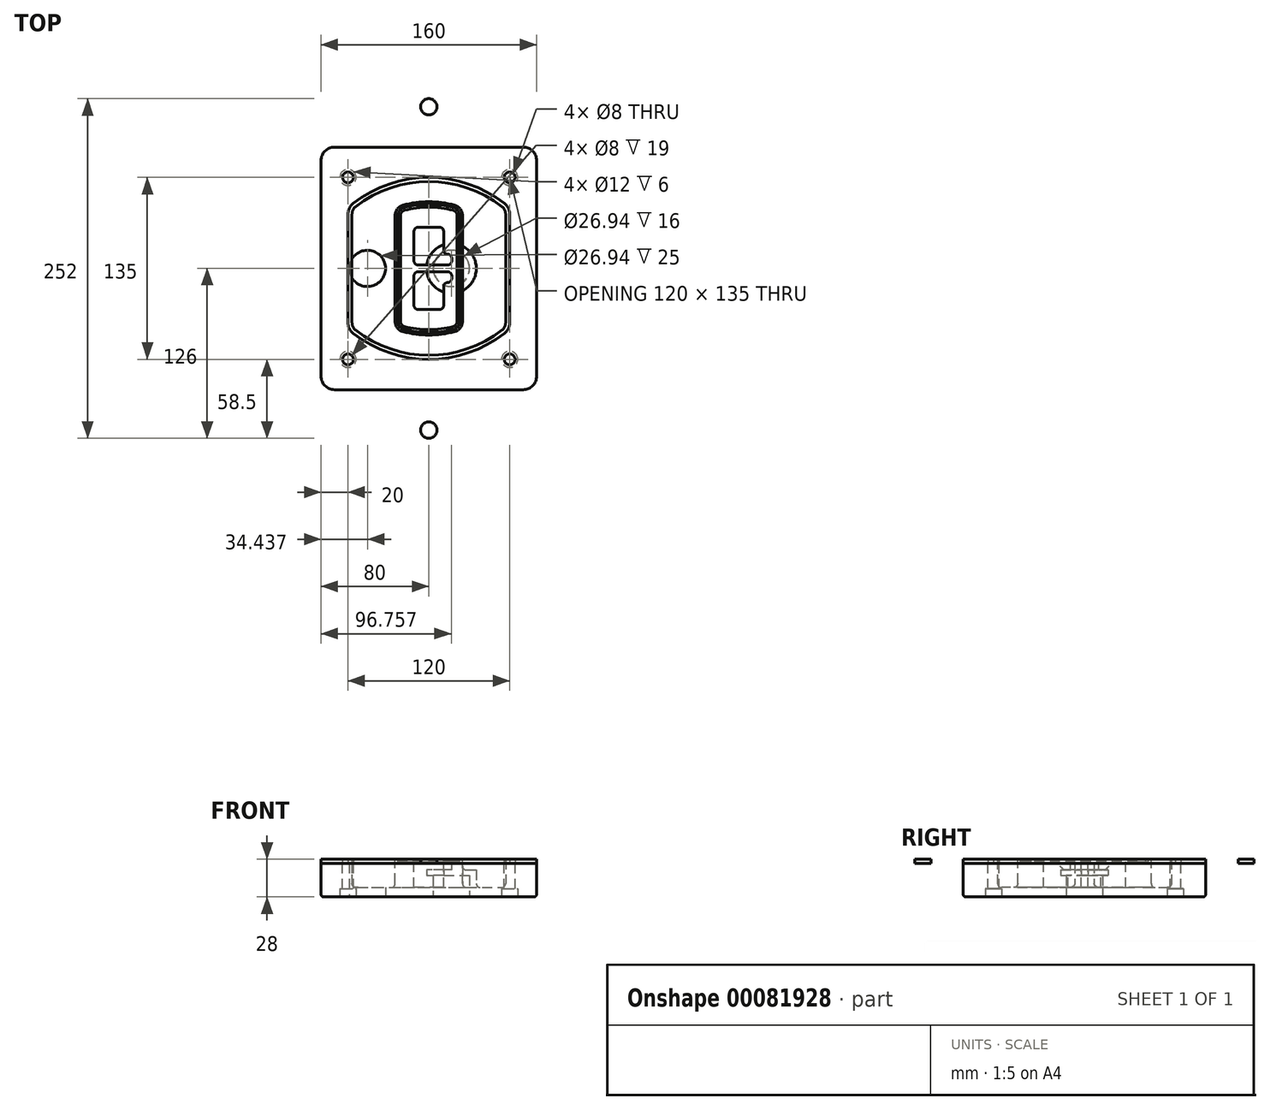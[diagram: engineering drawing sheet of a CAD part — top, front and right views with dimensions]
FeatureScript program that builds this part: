
annotation { "Feature Type Name" : "Feature", "Feature Type Description" : "" }
export const myFeature = defineFeature(function(context is Context, id is Id, definition is map)
    precondition{}
    {
        {
            var Q0;
            Q0=qCreatedBy(makeId("Top.planeOp"),FACE);
            var sketch = newSketch(context, id + "F0", { "sketchPlane" : qUnion([Q0])});
            skPoint(sketch, "E0.rect.middle", {"position": v(0, 0) * mm});
            skLineSegment(sketch, "E1.bottom", {"start": v(-70, -90) * mm, "end": v(70, -90) * mm});
            skLineSegment(sketch, "E1.top", {"start": v(-70, 90) * mm, "end": v(70, 90) * mm});
            skLineSegment(sketch, "E1.left", {"start": v(-80, -80) * mm, "end": v(-80, 80) * mm});
            skLineSegment(sketch, "E1.right", {"start": v(80, -80) * mm, "end": v(80, 80) * mm});
            skLineSegment(sketch, "E2", {"start": v(-80, 90) * mm, "end": v(80, -90) * mm, "construction": true});
            skLineSegment(sketch, "E3", {"start": v(80, 90) * mm, "end": v(-80, -90) * mm, "construction": true});
            skCircle(sketch, "E4", {"center": v(-60, 67.5) * mm, "radius": 4 * mm});
            skCircle(sketch, "E5", {"center": v(60, 67.5) * mm, "radius": 4 * mm});
            skCircle(sketch, "E6", {"center": v(60, -67.5) * mm, "radius": 4 * mm});
            skCircle(sketch, "E7", {"center": v(-60, -67.5) * mm, "radius": 4 * mm});
            skLineSegment(sketch, "E8", {"start": v(-60, 67.5) * mm, "end": v(60, 67.5) * mm, "construction": true});
            skLineSegment(sketch, "E9", {"start": v(60, 67.5) * mm, "end": v(60, -67.5) * mm, "construction": true});
            skLineSegment(sketch, "E10", {"start": v(60, -67.5) * mm, "end": v(-60, -67.5) * mm, "construction": true});
            skLineSegment(sketch, "E11", {"start": v(-60, -67.5) * mm, "end": v(-60, 67.5) * mm, "construction": true});
            skLineSegment(sketch, "E12", {"start": v(-60, 40.3) * mm, "end": v(-60, -40.3) * mm});
            skLineSegment(sketch, "E13", {"start": v(60, 40.3) * mm, "end": v(60, -40.3) * mm});
            skArc(sketch, "E14", {"start": v(56.15, 48.18) * mm, "mid": v(0, 67.5) * mm, "end": v(-56.15, 48.18) * mm});
            skArc(sketch, "E15", {"start": v(-56.15, -48.18) * mm, "mid": v(0, -67.5) * mm, "end": v(56.15, -48.18) * mm});
            skLineSegment(sketch, "E16", {"start": v(-60, 0) * mm, "end": v(60, 0) * mm, "construction": true});
            skPoint(sketch, "E17.visualSharp", {"position": v(-60, -45) * mm});
            skArc(sketch, "E17.filletArc", {"start": v(-60, -40.3) * mm, "mid": v(-58.99, -44.68) * mm, "end": v(-56.15, -48.18) * mm});
            skPoint(sketch, "E18.visualSharp", {"position": v(-60, 45) * mm});
            skArc(sketch, "E18.filletArc", {"start": v(-56.15, 48.18) * mm, "mid": v(-58.99, 44.68) * mm, "end": v(-60, 40.3) * mm});
            skPoint(sketch, "E19.visualSharp", {"position": v(60, 45) * mm});
            skArc(sketch, "E19.filletArc", {"start": v(60, 40.3) * mm, "mid": v(58.99, 44.68) * mm, "end": v(56.15, 48.18) * mm});
            skPoint(sketch, "E20.visualSharp", {"position": v(60, -45) * mm});
            skArc(sketch, "E20.filletArc", {"start": v(56.15, -48.18) * mm, "mid": v(58.99, -44.68) * mm, "end": v(60, -40.3) * mm});
            skPoint(sketch, "E21.visualSharp", {"position": v(-80, 90) * mm});
            skArc(sketch, "E21.filletArc", {"start": v(-70, 90) * mm, "mid": v(-77.07, 87.07) * mm, "end": v(-80, 80) * mm});
            skPoint(sketch, "E22.visualSharp", {"position": v(80, 90) * mm});
            skArc(sketch, "E22.filletArc", {"start": v(80, 80) * mm, "mid": v(77.07, 87.07) * mm, "end": v(70, 90) * mm});
            skPoint(sketch, "E23.visualSharp", {"position": v(80, -90) * mm});
            skArc(sketch, "E23.filletArc", {"start": v(70, -90) * mm, "mid": v(77.07, -87.07) * mm, "end": v(80, -80) * mm});
            skPoint(sketch, "E24.visualSharp", {"position": v(-80, -90) * mm});
            skArc(sketch, "E24.filletArc", {"start": v(-80, -80) * mm, "mid": v(-77.07, -87.07) * mm, "end": v(-70, -90) * mm});
            skArc(sketch, "E25.0", {"start": v(57, 40.3) * mm, "mid": v(56.3, 43.36) * mm, "end": v(54.3, 45.81) * mm});
            skLineSegment(sketch, "E25.1", {"start": v(57, 40.3) * mm, "end": v(57, -40.3) * mm});
            skArc(sketch, "E25.2", {"start": v(54.3, -45.81) * mm, "mid": v(56.3, -43.36) * mm, "end": v(57, -40.3) * mm});
            skArc(sketch, "E25.3", {"start": v(-54.3, -45.81) * mm, "mid": v(0, -64.5) * mm, "end": v(54.3, -45.81) * mm});
            skArc(sketch, "E25.4", {"start": v(-57, -40.3) * mm, "mid": v(-56.3, -43.36) * mm, "end": v(-54.3, -45.81) * mm});
            skArc(sketch, "E25.5", {"start": v(54.3, 45.81) * mm, "mid": v(0, 64.5) * mm, "end": v(-54.3, 45.81) * mm});
            skLineSegment(sketch, "E25.6", {"start": v(-57, 40.3) * mm, "end": v(-57, -40.3) * mm});
            skArc(sketch, "E25.7", {"start": v(-54.3, 45.81) * mm, "mid": v(-56.3, 43.36) * mm, "end": v(-57, 40.3) * mm});
            skArc(sketch, "E26.0", {"start": v(-58.62, 51.33) * mm, "mid": v(-62.58, 46.43) * mm, "end": v(-64, 40.3) * mm});
            skArc(sketch, "E26.1", {"start": v(58.62, 51.33) * mm, "mid": v(0, 71.5) * mm, "end": v(-58.62, 51.33) * mm});
            skArc(sketch, "E26.2", {"start": v(64, 40.3) * mm, "mid": v(62.58, 46.43) * mm, "end": v(58.62, 51.33) * mm});
            skLineSegment(sketch, "E26.3", {"start": v(64, 40.3) * mm, "end": v(64, -40.3) * mm});
            skArc(sketch, "E26.4", {"start": v(58.62, -51.33) * mm, "mid": v(62.58, -46.43) * mm, "end": v(64, -40.3) * mm});
            skLineSegment(sketch, "E26.5", {"start": v(-64, 40.3) * mm, "end": v(-64, -40.3) * mm});
            skArc(sketch, "E26.6", {"start": v(-58.62, -51.33) * mm, "mid": v(0, -71.5) * mm, "end": v(58.62, -51.33) * mm});
            skArc(sketch, "E26.7", {"start": v(-64, -40.3) * mm, "mid": v(-62.58, -46.43) * mm, "end": v(-58.62, -51.33) * mm});
            skSolve(sketch);
        }
        {
            var Q0;
            Q0=makeQuery(id+"F0.imprint","IMPRINT",FACE,{"disambiguationData":[TD([[makeQuery(id+"F0.imprint","IMPRINT",EDGE,{"derivedFrom":sQuery(id+"F0.wireOp",EDGE,"E1.bottom")}),1.0]])]});
            var Q1;
            Q1=makeQuery(id+"F0.imprint","IMPRINT",FACE,{"disambiguationData":[TD([[makeQuery(id+"F0.imprint","IMPRINT",EDGE,{"derivedFrom":sQuery(id+"F0.wireOp",EDGE,"E12")}),1.0]])]});
            var Q2;
            Q2=makeQuery(id+"F0.imprint","IMPRINT",FACE,{"disambiguationData":[TD([[makeQuery(id+"F0.imprint","IMPRINT",EDGE,{"derivedFrom":sQuery(id+"F0.wireOp",EDGE,"E25.0")}),1.0]])]});
            var Q3;
            Q3=makeQuery(id+"F0.imprint","IMPRINT",FACE,{"disambiguationData":[TD([[makeQuery(id+"F0.imprint","IMPRINT",EDGE,{"derivedFrom":sQuery(id+"F0.wireOp",EDGE,"E12")}),-1.0]])]});
            extrude(context, id + "F1", {"entities" : qUnion([Q0, Q1, Q2, Q3]), "oppositeDirection" : true, "depth" : 25 * mm});
        }
        {
            var Q0;
            Q0=makeQuery(id+"F0.imprint","IMPRINT",FACE,{"disambiguationData":[TD([[makeQuery(id+"F0.imprint","IMPRINT",EDGE,{"derivedFrom":sQuery(id+"F0.wireOp",EDGE,"E12")}),1.0]])]});
            extrude(context, id + "F2", {"entities" : qUnion([Q0]), "operationType" : NewBodyOperationType.ADD, "depth" : 3 * mm});
        }
        {
            var Q0;
            Q0=makeQuery(id+"F0.imprint","IMPRINT",FACE,{"disambiguationData":[TD([[makeQuery(id+"F0.imprint","IMPRINT",EDGE,{"derivedFrom":sQuery(id+"F0.wireOp",EDGE,"E25.0")}),1.0]])]});
            extrude(context, id + "F3", {"entities" : qUnion([Q0]), "operationType" : NewBodyOperationType.REMOVE, "oppositeDirection" : true, "depth" : 18 * mm});
        }
        {
            var Q0;
            Q0=makeQuery(id+"F2.opExtrude","CAP_FACE",FACE,{"disambiguationData":[OSD([sQuery(id+"F0.wireOp",EDGE,"E12"),sQuery(id+"F0.wireOp",EDGE,"E13"),sQuery(id+"F0.wireOp",EDGE,"E14"),sQuery(id+"F0.wireOp",EDGE,"E15"),sQuery(id+"F0.wireOp",EDGE,"E17.filletArc"),sQuery(id+"F0.wireOp",EDGE,"E18.filletArc"),sQuery(id+"F0.wireOp",EDGE,"E19.filletArc"),sQuery(id+"F0.wireOp",EDGE,"E20.filletArc"),sQuery(id+"F0.wireOp",EDGE,"E25.0"),sQuery(id+"F0.wireOp",EDGE,"E25.1"),sQuery(id+"F0.wireOp",EDGE,"E25.2"),sQuery(id+"F0.wireOp",EDGE,"E25.3"),sQuery(id+"F0.wireOp",EDGE,"E25.4"),sQuery(id+"F0.wireOp",EDGE,"E25.5"),sQuery(id+"F0.wireOp",EDGE,"E25.6"),sQuery(id+"F0.wireOp",EDGE,"E25.7")])],"isStart":false});
            var sketch = newSketch(context, id + "F4", { "sketchPlane" : qUnion([Q0])});
            skArc(sketch, "E27.0", {"start": v(-19.08, -46.97) * mm, "mid": v(0, -49.5) * mm, "end": v(19.08, -46.97) * mm});
            skArc(sketch, "E28.0", {"start": v(19.08, 46.97) * mm, "mid": v(0, 49.5) * mm, "end": v(-19.08, 46.97) * mm});
            skLineSegment(sketch, "E29", {"start": v(-25, 39.25) * mm, "end": v(-25, -39.25) * mm});
            skLineSegment(sketch, "E30", {"start": v(25, 39.25) * mm, "end": v(25, -39.25) * mm});
            skLineSegment(sketch, "E31", {"start": v(-25, 45.1) * mm, "end": v(25, 45.1) * mm, "construction": true});
            skLineSegment(sketch, "E32", {"start": v(-25, -45.1) * mm, "end": v(25, -45.1) * mm, "construction": true});
            skPoint(sketch, "E33.visualSharp", {"position": v(-25, 45.1) * mm});
            skArc(sketch, "E33.filletArc", {"start": v(-19.08, 46.97) * mm, "mid": v(-23.35, 44.11) * mm, "end": v(-25, 39.25) * mm});
            skPoint(sketch, "E34.visualSharp", {"position": v(25, 45.1) * mm});
            skArc(sketch, "E34.filletArc", {"start": v(25, 39.25) * mm, "mid": v(23.35, 44.11) * mm, "end": v(19.08, 46.97) * mm});
            skPoint(sketch, "E35.visualSharp", {"position": v(25, -45.1) * mm});
            skArc(sketch, "E35.filletArc", {"start": v(19.08, -46.97) * mm, "mid": v(23.35, -44.11) * mm, "end": v(25, -39.25) * mm});
            skPoint(sketch, "E36.visualSharp", {"position": v(-25, -45.1) * mm});
            skArc(sketch, "E36.filletArc", {"start": v(-25, -39.25) * mm, "mid": v(-23.35, -44.11) * mm, "end": v(-19.08, -46.97) * mm});
            skArc(sketch, "E37.0", {"start": v(54.3, 45.81) * mm, "mid": v(0, 64.5) * mm, "end": v(-54.3, 45.81) * mm});
            skArc(sketch, "E37.1", {"start": v(-54.3, 45.81) * mm, "mid": v(-56.3, 43.36) * mm, "end": v(-57, 40.3) * mm});
            skLineSegment(sketch, "E37.2", {"start": v(-57, 40.3) * mm, "end": v(-57, -40.3) * mm});
            skArc(sketch, "E37.3", {"start": v(-57, -40.3) * mm, "mid": v(-56.3, -43.36) * mm, "end": v(-54.3, -45.81) * mm});
            skArc(sketch, "E37.4", {"start": v(-54.3, -45.81) * mm, "mid": v(0, -64.5) * mm, "end": v(54.3, -45.81) * mm});
            skArc(sketch, "E37.5", {"start": v(54.3, -45.81) * mm, "mid": v(56.3, -43.36) * mm, "end": v(57, -40.3) * mm});
            skLineSegment(sketch, "E37.6", {"start": v(57, 40.3) * mm, "end": v(57, -40.3) * mm});
            skArc(sketch, "E37.7", {"start": v(57, 40.3) * mm, "mid": v(56.3, 43.36) * mm, "end": v(54.3, 45.81) * mm});
            skLineSegment(sketch, "E38.0", {"start": v(23, 39.25) * mm, "end": v(23, -39.25) * mm});
            skArc(sketch, "E38.1", {"start": v(18.56, -45.04) * mm, "mid": v(21.76, -42.9) * mm, "end": v(23, -39.25) * mm});
            skArc(sketch, "E38.2", {"start": v(-18.56, -45.04) * mm, "mid": v(0, -47.5) * mm, "end": v(18.56, -45.04) * mm});
            skArc(sketch, "E38.3", {"start": v(-23, -39.25) * mm, "mid": v(-21.76, -42.9) * mm, "end": v(-18.56, -45.04) * mm});
            skLineSegment(sketch, "E38.4", {"start": v(-23, 39.25) * mm, "end": v(-23, -39.25) * mm});
            skArc(sketch, "E38.5", {"start": v(23, 39.25) * mm, "mid": v(21.76, 42.9) * mm, "end": v(18.56, 45.04) * mm});
            skArc(sketch, "E38.6", {"start": v(-18.56, 45.04) * mm, "mid": v(-21.76, 42.9) * mm, "end": v(-23, 39.25) * mm});
            skArc(sketch, "E38.7", {"start": v(18.56, 45.04) * mm, "mid": v(0, 47.5) * mm, "end": v(-18.56, 45.04) * mm});
            skArc(sketch, "E39.0", {"start": v(21, 39.25) * mm, "mid": v(20.18, 41.68) * mm, "end": v(18.04, 43.1) * mm});
            skLineSegment(sketch, "E39.1", {"start": v(21, 39.25) * mm, "end": v(21, -39.25) * mm});
            skArc(sketch, "E39.2", {"start": v(18.04, -43.1) * mm, "mid": v(20.18, -41.68) * mm, "end": v(21, -39.25) * mm});
            skArc(sketch, "E39.3", {"start": v(-18.04, -43.1) * mm, "mid": v(0, -45.5) * mm, "end": v(18.04, -43.1) * mm});
            skArc(sketch, "E39.4", {"start": v(-21, -39.25) * mm, "mid": v(-20.18, -41.68) * mm, "end": v(-18.04, -43.1) * mm});
            skArc(sketch, "E39.5", {"start": v(18.04, 43.1) * mm, "mid": v(0, 45.5) * mm, "end": v(-18.04, 43.1) * mm});
            skLineSegment(sketch, "E39.6", {"start": v(-21, 39.25) * mm, "end": v(-21, -39.25) * mm});
            skArc(sketch, "E39.7", {"start": v(-18.04, 43.1) * mm, "mid": v(-20.18, 41.68) * mm, "end": v(-21, 39.25) * mm});
            skLineSegment(sketch, "E40", {"start": v(-25, 0) * mm, "end": v(25, 0) * mm, "construction": true});
            skLineSegment(sketch, "E41", {"start": v(-11, 5.5) * mm, "end": v(-11, 27.5) * mm});
            skLineSegment(sketch, "E42", {"start": v(-8, 30.5) * mm, "end": v(8, 30.5) * mm});
            skLineSegment(sketch, "E43", {"start": v(11, 27.5) * mm, "end": v(11, 13.5) * mm});
            skLineSegment(sketch, "E44", {"start": v(14, 10.5) * mm, "end": v(14, 10.5) * mm});
            skLineSegment(sketch, "E45", {"start": v(17, 7.5) * mm, "end": v(17, 5.5) * mm});
            skLineSegment(sketch, "E46", {"start": v(14, 2.5) * mm, "end": v(-8, 2.5) * mm});
            skPoint(sketch, "E47.visualSharp", {"position": v(-11, 30.5) * mm});
            skArc(sketch, "E47.filletArc", {"start": v(-8, 30.5) * mm, "mid": v(-10.12, 29.62) * mm, "end": v(-11, 27.5) * mm});
            skPoint(sketch, "E48.visualSharp", {"position": v(11, 30.5) * mm});
            skArc(sketch, "E48.filletArc", {"start": v(11, 27.5) * mm, "mid": v(10.12, 29.62) * mm, "end": v(8, 30.5) * mm});
            skPoint(sketch, "E49.visualSharp", {"position": v(11, 10.5) * mm});
            skArc(sketch, "E49.filletArc", {"start": v(11, 13.5) * mm, "mid": v(11.88, 11.38) * mm, "end": v(14, 10.5) * mm});
            skPoint(sketch, "E50.visualSharp", {"position": v(17, 10.5) * mm});
            skArc(sketch, "E50.filletArc", {"start": v(17, 7.5) * mm, "mid": v(16.12, 9.62) * mm, "end": v(14, 10.5) * mm});
            skPoint(sketch, "E51.visualSharp", {"position": v(17, 2.5) * mm});
            skArc(sketch, "E51.filletArc", {"start": v(14, 2.5) * mm, "mid": v(16.12, 3.38) * mm, "end": v(17, 5.5) * mm});
            skPoint(sketch, "E52.visualSharp", {"position": v(-11, 2.5) * mm});
            skArc(sketch, "E52.filletArc", {"start": v(-11, 5.5) * mm, "mid": v(-10.12, 3.38) * mm, "end": v(-8, 2.5) * mm});
            skLineSegment(sketch, "E53.0.MirrorCS", {"start": v(14, -2.5) * mm, "end": v(-8, -2.5) * mm});
            skArc(sketch, "E54.0.MirrorCS", {"start": v(-11, -5.5) * mm, "mid": v(-10.12, -3.38) * mm, "end": v(-8, -2.5) * mm});
            skLineSegment(sketch, "E55.0.MirrorCS", {"start": v(-11, -5.5) * mm, "end": v(-11, -27.5) * mm});
            skArc(sketch, "E56.0.MirrorCS", {"start": v(-8, -30.5) * mm, "mid": v(-10.12, -29.62) * mm, "end": v(-11, -27.5) * mm});
            skLineSegment(sketch, "E57.0.MirrorCS", {"start": v(-8, -30.5) * mm, "end": v(8, -30.5) * mm});
            skArc(sketch, "E58.0.MirrorCS", {"start": v(11, -27.5) * mm, "mid": v(10.12, -29.62) * mm, "end": v(8, -30.5) * mm});
            skLineSegment(sketch, "E59.0.MirrorCS", {"start": v(11, -27.5) * mm, "end": v(11, -13.5) * mm});
            skArc(sketch, "E60.0.MirrorCS", {"start": v(11, -13.5) * mm, "mid": v(11.88, -11.38) * mm, "end": v(14, -10.5) * mm});
            skArc(sketch, "E61.0.MirrorCS", {"start": v(17, -7.5) * mm, "mid": v(16.12, -9.62) * mm, "end": v(14, -10.5) * mm});
            skLineSegment(sketch, "E62.0.MirrorCS", {"start": v(17, -7.5) * mm, "end": v(17, -5.5) * mm});
            skArc(sketch, "E63.0.MirrorCS", {"start": v(14, -2.5) * mm, "mid": v(16.12, -3.38) * mm, "end": v(17, -5.5) * mm});
            skSolve(sketch);
        }
        {
            var Q0;
            Q0=makeQuery(id+"F4.imprint","IMPRINT",FACE,{"disambiguationData":[TD([[makeQuery(id+"F4.imprint","IMPRINT",EDGE,{"derivedFrom":sQuery(id+"F4.wireOp",EDGE,"E27.0")}),1.0]])]});
            var Q1;
            Q1=makeQuery(id+"F4.imprint","IMPRINT",FACE,{"disambiguationData":[TD([[makeQuery(id+"F4.imprint","IMPRINT",EDGE,{"derivedFrom":sQuery(id+"F4.wireOp",EDGE,"E38.0")}),-1.0]])]});
            var Q2;
            Q2=makeQuery(id+"F4.imprint","IMPRINT",FACE,{"disambiguationData":[TD([[makeQuery(id+"F4.imprint","IMPRINT",EDGE,{"derivedFrom":sQuery(id+"F4.wireOp",EDGE,"E39.0")}),1.0]])]});
            extrude(context, id + "F5", {"entities" : qUnion([Q0, Q1, Q2]), "operationType" : NewBodyOperationType.ADD, "endBound" : BoundingType.UP_TO_NEXT, "oppositeDirection" : true, "depth" : 25 * mm});
        }
        {
            var Q0;
            Q0=makeQuery(id+"F4.imprint","IMPRINT",FACE,{"disambiguationData":[TD([[makeQuery(id+"F4.imprint","IMPRINT",EDGE,{"derivedFrom":sQuery(id+"F4.wireOp",EDGE,"E38.0")}),-1.0]])]});
            extrude(context, id + "F6", {"entities" : qUnion([Q0]), "operationType" : NewBodyOperationType.REMOVE, "oppositeDirection" : true, "depth" : 2 * mm});
        }
        {
            var Q0;
            Q0=makeQuery(id+"F1.opExtrude","CAP_FACE",FACE,{"disambiguationData":[OSD([sQuery(id+"F0.wireOp",EDGE,"E1.bottom"),sQuery(id+"F0.wireOp",EDGE,"E1.top"),sQuery(id+"F0.wireOp",EDGE,"E1.left"),sQuery(id+"F0.wireOp",EDGE,"E1.right"),sQuery(id+"F0.wireOp",EDGE,"E4"),sQuery(id+"F0.wireOp",EDGE,"E5"),sQuery(id+"F0.wireOp",EDGE,"E6"),sQuery(id+"F0.wireOp",EDGE,"E7"),sQuery(id+"F0.wireOp",EDGE,"E21.filletArc"),sQuery(id+"F0.wireOp",EDGE,"E22.filletArc"),sQuery(id+"F0.wireOp",EDGE,"E23.filletArc"),sQuery(id+"F0.wireOp",EDGE,"E24.filletArc")])],"isStart":false});
            var sketch = newSketch(context, id + "F7", { "sketchPlane" : qUnion([Q0])});
            skCircle(sketch, "E64", {"center": v(16.76, 0) * mm, "radius": 13.47 * mm});
            skCircle(sketch, "E65", {"center": v(-45.56, 0) * mm, "radius": 13.47 * mm});
            skLineSegment(sketch, "E66", {"start": v(80, 0) * mm, "end": v(-80, 0) * mm});
            skCircle(sketch, "E67", {"center": v(16.76, 0) * mm, "radius": 18.47 * mm});
            skCircle(sketch, "E68", {"center": v(60, -67.5) * mm, "radius": 6 * mm});
            skCircle(sketch, "E69", {"center": v(-60, -67.5) * mm, "radius": 6 * mm});
            skCircle(sketch, "E70", {"center": v(-60, 67.5) * mm, "radius": 6 * mm});
            skCircle(sketch, "E71", {"center": v(60, 67.5) * mm, "radius": 6 * mm});
            skSolve(sketch);
        }
        {
            var Q0;
            {var subQ1=sQuery(id+"F7.wireOp",EDGE,"E66");var subQ4=sQuery(id+"F7.wireOp",EDGE,"E64");var subQ6=makeQuery(id+"F7.imprint","INTERSECT",VERTEX,{"disambiguationData":[OD(0.0)],"derivedFrom":[subQ4,subQ1]});Q0=makeQuery(id+"F7.imprint","IMPRINT",FACE,{"disambiguationData":[TD([[makeQuery(id+"F7.imprint","IMPRINT",EDGE,{"disambiguationData":[TD([[subQ6,-1.0]])],"derivedFrom":subQ4}),-1.0]])]});}
            var Q1;
            {var subQ0=sQuery(id+"F7.wireOp",EDGE,"E66");var subQ1=sQuery(id+"F7.wireOp",EDGE,"E64");var subQ3=makeQuery(id+"F7.imprint","INTERSECT",VERTEX,{"disambiguationData":[OD(0.0)],"derivedFrom":[subQ1,subQ0]});Q1=makeQuery(id+"F7.imprint","IMPRINT",FACE,{"disambiguationData":[TD([[makeQuery(id+"F7.imprint","IMPRINT",EDGE,{"disambiguationData":[TD([[subQ3,-1.0]])],"derivedFrom":subQ1}),1.0]])]});}
            var Q2;
            {var subQ0=sQuery(id+"F7.wireOp",EDGE,"E66");var subQ1=sQuery(id+"F7.wireOp",EDGE,"E64");var subQ3=makeQuery(id+"F7.imprint","INTERSECT",VERTEX,{"disambiguationData":[OD(0.0)],"derivedFrom":[subQ1,subQ0]});Q2=makeQuery(id+"F7.imprint","IMPRINT",FACE,{"disambiguationData":[TD([[makeQuery(id+"F7.imprint","IMPRINT",EDGE,{"disambiguationData":[TD([[subQ3,1.0]])],"derivedFrom":subQ1}),1.0]])]});}
            var Q3;
            {var subQ1=sQuery(id+"F7.wireOp",EDGE,"E66");var subQ4=sQuery(id+"F7.wireOp",EDGE,"E64");var subQ6=makeQuery(id+"F7.imprint","INTERSECT",VERTEX,{"disambiguationData":[OD(0.0)],"derivedFrom":[subQ4,subQ1]});Q3=makeQuery(id+"F7.imprint","IMPRINT",FACE,{"disambiguationData":[TD([[makeQuery(id+"F7.imprint","IMPRINT",EDGE,{"disambiguationData":[TD([[subQ6,1.0]])],"derivedFrom":subQ4}),-1.0]])]});}
            extrude(context, id + "F8", {"entities" : qUnion([Q0, Q1, Q2, Q3]), "operationType" : NewBodyOperationType.ADD, "oppositeDirection" : true, "depth" : 20 * mm});
        }
        {
            var Q0;
            {var subQ0=sQuery(id+"F7.wireOp",EDGE,"E66");var subQ1=sQuery(id+"F7.wireOp",EDGE,"E64");var subQ3=makeQuery(id+"F7.imprint","INTERSECT",VERTEX,{"disambiguationData":[OD(0.0)],"derivedFrom":[subQ1,subQ0]});Q0=makeQuery(id+"F7.imprint","IMPRINT",FACE,{"disambiguationData":[TD([[makeQuery(id+"F7.imprint","IMPRINT",EDGE,{"disambiguationData":[TD([[subQ3,-1.0]])],"derivedFrom":subQ1}),1.0]])]});}
            var Q1;
            {var subQ0=sQuery(id+"F7.wireOp",EDGE,"E66");var subQ1=sQuery(id+"F7.wireOp",EDGE,"E64");var subQ3=makeQuery(id+"F7.imprint","INTERSECT",VERTEX,{"disambiguationData":[OD(0.0)],"derivedFrom":[subQ1,subQ0]});Q1=makeQuery(id+"F7.imprint","IMPRINT",FACE,{"disambiguationData":[TD([[makeQuery(id+"F7.imprint","IMPRINT",EDGE,{"disambiguationData":[TD([[subQ3,1.0]])],"derivedFrom":subQ1}),1.0]])]});}
            extrude(context, id + "F9", {"entities" : qUnion([Q0, Q1]), "operationType" : NewBodyOperationType.REMOVE, "oppositeDirection" : true, "depth" : 16 * mm});
        }
        {
            var Q0;
            {var subQ0=sQuery(id+"F7.wireOp",EDGE,"E66");var subQ1=sQuery(id+"F7.wireOp",EDGE,"E65");var subQ3=makeQuery(id+"F7.imprint","INTERSECT",VERTEX,{"disambiguationData":[OD(0.0)],"derivedFrom":[subQ1,subQ0]});Q0=makeQuery(id+"F7.imprint","IMPRINT",FACE,{"disambiguationData":[TD([[makeQuery(id+"F7.imprint","IMPRINT",EDGE,{"disambiguationData":[TD([[subQ3,-1.0]])],"derivedFrom":subQ1}),1.0]])]});}
            var Q1;
            {var subQ0=sQuery(id+"F7.wireOp",EDGE,"E66");var subQ1=sQuery(id+"F7.wireOp",EDGE,"E65");var subQ3=makeQuery(id+"F7.imprint","INTERSECT",VERTEX,{"disambiguationData":[OD(0.0)],"derivedFrom":[subQ1,subQ0]});Q1=makeQuery(id+"F7.imprint","IMPRINT",FACE,{"disambiguationData":[TD([[makeQuery(id+"F7.imprint","IMPRINT",EDGE,{"disambiguationData":[TD([[subQ3,1.0]])],"derivedFrom":subQ1}),1.0]])]});}
            extrude(context, id + "F10", {"entities" : qUnion([Q0, Q1]), "operationType" : NewBodyOperationType.REMOVE, "oppositeDirection" : true, "depth" : 25 * mm});
        }
        {
            var Q0;
            Q0=makeQuery(id+"F7.imprint","IMPRINT",FACE,{"disambiguationData":[TD([[makeQuery(id+"F7.imprint","IMPRINT",EDGE,{"derivedFrom":sQuery(id+"F7.wireOp",EDGE,"E68")}),1.0]])]});
            var Q1;
            Q1=makeQuery(id+"F7.imprint","IMPRINT",FACE,{"disambiguationData":[TD([[makeQuery(id+"F7.imprint","IMPRINT",EDGE,{"derivedFrom":makeQuery(id+"F1.opExtrude","CAP_EDGE",EDGE,{"disambiguationData":[OSD([sQuery(id+"F0.wireOp",EDGE,"E5")])],"isStart":false})}),-1.0]])]});
            var Q2;
            Q2=makeQuery(id+"F7.imprint","IMPRINT",FACE,{"disambiguationData":[TD([[makeQuery(id+"F7.imprint","IMPRINT",EDGE,{"derivedFrom":sQuery(id+"F7.wireOp",EDGE,"E69")}),1.0]])]});
            var Q3;
            Q3=makeQuery(id+"F7.imprint","IMPRINT",FACE,{"disambiguationData":[TD([[makeQuery(id+"F7.imprint","IMPRINT",EDGE,{"derivedFrom":makeQuery(id+"F1.opExtrude","CAP_EDGE",EDGE,{"disambiguationData":[OSD([sQuery(id+"F0.wireOp",EDGE,"E4")])],"isStart":false})}),-1.0]])]});
            var Q4;
            Q4=makeQuery(id+"F7.imprint","IMPRINT",FACE,{"disambiguationData":[TD([[makeQuery(id+"F7.imprint","IMPRINT",EDGE,{"derivedFrom":sQuery(id+"F7.wireOp",EDGE,"E70")}),1.0]])]});
            var Q5;
            Q5=makeQuery(id+"F7.imprint","IMPRINT",FACE,{"disambiguationData":[TD([[makeQuery(id+"F7.imprint","IMPRINT",EDGE,{"derivedFrom":makeQuery(id+"F1.opExtrude","CAP_EDGE",EDGE,{"disambiguationData":[OSD([sQuery(id+"F0.wireOp",EDGE,"E7")])],"isStart":false})}),-1.0]])]});
            var Q6;
            Q6=makeQuery(id+"F7.imprint","IMPRINT",FACE,{"disambiguationData":[TD([[makeQuery(id+"F7.imprint","IMPRINT",EDGE,{"derivedFrom":sQuery(id+"F7.wireOp",EDGE,"E71")}),1.0]])]});
            var Q7;
            Q7=makeQuery(id+"F7.imprint","IMPRINT",FACE,{"disambiguationData":[TD([[makeQuery(id+"F7.imprint","IMPRINT",EDGE,{"derivedFrom":makeQuery(id+"F1.opExtrude","CAP_EDGE",EDGE,{"disambiguationData":[OSD([sQuery(id+"F0.wireOp",EDGE,"E6")])],"isStart":false})}),-1.0]])]});
            extrude(context, id + "F11", {"entities" : qUnion([Q0, Q1, Q2, Q3, Q4, Q5, Q6, Q7]), "operationType" : NewBodyOperationType.REMOVE, "oppositeDirection" : true, "depth" : 6 * mm});
        }
        {
            var Q0;
            Q0=makeQuery(id+"F9.boolean.opBoolean","COPY",FACE,{"derivedFrom":makeQuery(id+"F9.opExtrude","CAP_FACE",FACE,{"disambiguationData":[OSD([sQuery(id+"F7.wireOp",EDGE,"E64")])],"isStart":false})});
            var sketch = newSketch(context, id + "F12", { "sketchPlane" : qUnion([Q0])});
            skArc(sketch, "E72.0", {"start": v(11, 17.55) * mm, "mid": v(2.57, 11.82) * mm, "end": v(-1.54, 2.5) * mm});
            skArc(sketch, "E72.1", {"start": v(-1.54, -2.5) * mm, "mid": v(2.57, -11.82) * mm, "end": v(11, -17.55) * mm});
            skLineSegment(sketch, "E73", {"start": v(-1.54, -2.5) * mm, "end": v(14, -2.5) * mm});
            skLineSegment(sketch, "E74.0", {"start": v(14, 2.5) * mm, "end": v(-1.54, 2.5) * mm});
            skArc(sketch, "E74.1", {"start": v(14, 2.5) * mm, "mid": v(16.12, 3.38) * mm, "end": v(17, 5.5) * mm});
            skLineSegment(sketch, "E74.2", {"start": v(17, 7.5) * mm, "end": v(17, 5.5) * mm});
            skArc(sketch, "E74.3", {"start": v(17, 7.5) * mm, "mid": v(16.12, 9.62) * mm, "end": v(14, 10.5) * mm});
            skArc(sketch, "E74.4", {"start": v(11, 13.5) * mm, "mid": v(11.88, 11.38) * mm, "end": v(14, 10.5) * mm});
            skLineSegment(sketch, "E74.5", {"start": v(11, 17.55) * mm, "end": v(11, 13.5) * mm});
            skLineSegment(sketch, "E74.7", {"start": v(14, -2.5) * mm, "end": v(-1.54, -2.5) * mm});
            skArc(sketch, "E74.8", {"start": v(14, -2.5) * mm, "mid": v(16.12, -3.38) * mm, "end": v(17, -5.5) * mm});
            skLineSegment(sketch, "E74.9", {"start": v(17, -7.5) * mm, "end": v(17, -5.5) * mm});
            skArc(sketch, "E74.10", {"start": v(17, -7.5) * mm, "mid": v(16.12, -9.62) * mm, "end": v(14, -10.5) * mm});
            skArc(sketch, "E74.11", {"start": v(11, -13.5) * mm, "mid": v(11.88, -11.38) * mm, "end": v(14, -10.5) * mm});
            skLineSegment(sketch, "E74.12", {"start": v(11, -17.55) * mm, "end": v(11, -13.5) * mm});
            skPoint(sketch, "E75.orphan", {"position": v(11, -27.5) * mm});
            skPoint(sketch, "E76.orphan", {"position": v(-8, -2.5) * mm});
            skPoint(sketch, "E77.orphan", {"position": v(-8, 2.5) * mm});
            skPoint(sketch, "E78.orphan", {"position": v(11, 27.5) * mm});
            skSolve(sketch);
        }
        {
            var Q0;
            {var subQ7=sQuery(id+"F12.wireOp",EDGE,"E72.0");var subQ14=sQuery(id+"F12.wireOp",EDGE,"E72.1");var subQ16=sQuery(id+"F12.wireOp",EDGE,"E74.1");var subQ18=sQuery(id+"F12.wireOp",EDGE,"E74.8");Q0=qUnion([makeQuery(id+"F12.imprint","IMPRINT",FACE,{"disambiguationData":[TD([[makeQuery(id+"F12.imprint","IMPRINT",EDGE,{"derivedFrom":subQ7}),1.0]])]}),makeQuery(id+"F12.imprint","IMPRINT",FACE,{"disambiguationData":[TD([[makeQuery(id+"F12.imprint","IMPRINT",EDGE,{"derivedFrom":subQ14}),1.0]])]}),makeQuery(id+"F12.imprint","IMPRINT",FACE,{"disambiguationData":[TD([[makeQuery(id+"F12.imprint","IMPRINT",EDGE,{"derivedFrom":subQ16}),1.0]])]}),makeQuery(id+"F12.imprint","IMPRINT",FACE,{"disambiguationData":[TD([[makeQuery(id+"F12.imprint","IMPRINT",EDGE,{"derivedFrom":subQ18}),-1.0]])]})]);}
            var Q1;
            Q1=makeQuery(id+"F5.boolean.opBoolean","SPLIT",FACE,{"disambiguationData":[TD([makeQuery(id+"F5.opExtrude","SWEPT_FACE",FACE,{"disambiguationData":[OSD([sQuery(id+"F4.wireOp",EDGE,"E41")])]})])],"derivedFrom":makeQuery(id+"F3.boolean.opBoolean","COPY",FACE,{"derivedFrom":makeQuery(id+"F3.opExtrude","CAP_FACE",FACE,{"disambiguationData":[OSD([sQuery(id+"F0.wireOp",EDGE,"E25.0"),sQuery(id+"F0.wireOp",EDGE,"E25.1"),sQuery(id+"F0.wireOp",EDGE,"E25.2"),sQuery(id+"F0.wireOp",EDGE,"E25.3"),sQuery(id+"F0.wireOp",EDGE,"E25.4"),sQuery(id+"F0.wireOp",EDGE,"E25.5"),sQuery(id+"F0.wireOp",EDGE,"E25.6"),sQuery(id+"F0.wireOp",EDGE,"E25.7")])],"isStart":false})})});
            extrude(context, id + "F13", {"entities" : qUnion([Q0]), "operationType" : NewBodyOperationType.REMOVE, "endBound" : BoundingType.UP_TO_SURFACE, "endBoundEntityFace" : qUnion([Q1]), "depth" : 25 * mm});
        }
        {
            var Q0;
            Q0=makeQuery(id+"F3.boolean.opBoolean","COPY",EDGE,{"derivedFrom":makeQuery(id+"F3.opExtrude","CAP_EDGE",EDGE,{"disambiguationData":[OSD([sQuery(id+"F0.wireOp",EDGE,"E25.6")])],"isStart":false})});
            var Q1;
            Q1=makeQuery(id+"F8.boolean.opBoolean","INTERSECT",EDGE,{"derivedFrom":[makeQuery(id+"F5.opExtrude","SWEPT_FACE",FACE,{"disambiguationData":[OSD([sQuery(id+"F4.wireOp",EDGE,"E30")])]}),makeQuery(id+"F8.opExtrude","CAP_FACE",FACE,{"disambiguationData":[OSD([sQuery(id+"F7.wireOp",EDGE,"E67")])],"isStart":false})]});
            var Q2;
            Q2=makeQuery(id+"F8.boolean.opBoolean","INTERSECT",EDGE,{"disambiguationData":[OD(1.0)],"derivedFrom":[makeQuery(id+"F5.opExtrude","SWEPT_FACE",FACE,{"disambiguationData":[OSD([sQuery(id+"F4.wireOp",EDGE,"E30")])]}),makeQuery(id+"F8.opExtrude","SWEPT_FACE",FACE,{"disambiguationData":[OSD([sQuery(id+"F7.wireOp",EDGE,"E67")])]})]});
            var Q3;
            {var subQ0=sQuery(id+"F4.wireOp",EDGE,"E30");Q3=makeQuery(id+"F8.boolean.opBoolean","SPLIT",EDGE,{"disambiguationData":[TD([makeQuery(id+"F5.opExtrude","SWEPT_FACE",FACE,{"disambiguationData":[OSD([sQuery(id+"F4.wireOp",EDGE,"E35.filletArc")])]})])],"derivedFrom":makeQuery(id+"F5.opExtrude","CAP_EDGE",EDGE,{"disambiguationData":[OSD([subQ0])],"isStart":false})});}
            var Q4;
            {var subQ0=sQuery(id+"F0.wireOp",EDGE,"E25.7");var subQ1=sQuery(id+"F0.wireOp",EDGE,"E25.1");var subQ2=sQuery(id+"F0.wireOp",EDGE,"E25.6");var subQ3=sQuery(id+"F0.wireOp",EDGE,"E25.5");var subQ4=sQuery(id+"F0.wireOp",EDGE,"E25.4");var subQ5=sQuery(id+"F0.wireOp",EDGE,"E25.0");var subQ6=sQuery(id+"F0.wireOp",EDGE,"E25.2");var subQ7=sQuery(id+"F0.wireOp",EDGE,"E25.3");Q4=makeQuery(id+"F8.boolean.opBoolean","INTERSECT",EDGE,{"derivedFrom":[makeQuery(id+"F5.boolean.opBoolean","SPLIT",FACE,{"disambiguationData":[TD([makeQuery(id+"F2.opExtrude","SWEPT_FACE",FACE,{"disambiguationData":[OSD([subQ5])]})])],"derivedFrom":makeQuery(id+"F3.boolean.opBoolean","COPY",FACE,{"derivedFrom":makeQuery(id+"F3.opExtrude","CAP_FACE",FACE,{"disambiguationData":[OSD([subQ5,subQ1,subQ6,subQ7,subQ4,subQ3,subQ2,subQ0])],"isStart":false})})}),makeQuery(id+"F8.opExtrude","SWEPT_FACE",FACE,{"disambiguationData":[OSD([sQuery(id+"F7.wireOp",EDGE,"E67")])]})]});}
            var Q5;
            Q5=makeQuery(id+"F8.boolean.opBoolean","INTERSECT",EDGE,{"disambiguationData":[OD(0.0)],"derivedFrom":[makeQuery(id+"F5.opExtrude","SWEPT_FACE",FACE,{"disambiguationData":[OSD([sQuery(id+"F4.wireOp",EDGE,"E30")])]}),makeQuery(id+"F8.opExtrude","SWEPT_FACE",FACE,{"disambiguationData":[OSD([sQuery(id+"F7.wireOp",EDGE,"E67")])]})]});
            fillet(context, id + "F14", {"entities" : qUnion([Q0, Q1, Q2, Q3, Q4, Q5]), "radius" : 3 * mm, "tangentPropagation" : true, "allowEdgeOverflow" : false});
        }
        {
            var Q0;
            Q0=makeQuery(id+"F1.opExtrude","CAP_EDGE",EDGE,{"disambiguationData":[OSD([sQuery(id+"F0.wireOp",EDGE,"E1.bottom")])],"isStart":false});
            fillet(context, id + "F15", {"entities" : qUnion([Q0]), "radius" : 2 * mm, "tangentPropagation" : true, "allowEdgeOverflow" : false});
        }
        {
            var Q0;
            {var subQ0=sQuery(id+"F0.wireOp",EDGE,"E22.filletArc");var subQ1=sQuery(id+"F0.wireOp",EDGE,"E7");var subQ2=sQuery(id+"F0.wireOp",EDGE,"E6");var subQ3=sQuery(id+"F0.wireOp",EDGE,"E5");var subQ4=sQuery(id+"F0.wireOp",EDGE,"E4");var subQ5=sQuery(id+"F0.wireOp",EDGE,"E1.bottom");var subQ6=sQuery(id+"F0.wireOp",EDGE,"E21.filletArc");var subQ7=sQuery(id+"F0.wireOp",EDGE,"E1.top");var subQ8=sQuery(id+"F0.wireOp",EDGE,"E1.left");var subQ9=sQuery(id+"F0.wireOp",EDGE,"E1.right");var subQ10=sQuery(id+"F0.wireOp",EDGE,"E23.filletArc");var subQ11=sQuery(id+"F0.wireOp",EDGE,"E24.filletArc");Q0=makeQuery(id+"F2.boolean.opBoolean","SPLIT",FACE,{"disambiguationData":[TD([makeQuery(id+"F1.opExtrude","SWEPT_FACE",FACE,{"disambiguationData":[OSD([subQ5])]})])],"derivedFrom":makeQuery(id+"F1.opExtrude","CAP_FACE",FACE,{"disambiguationData":[OSD([subQ5,subQ7,subQ8,subQ9,subQ4,subQ3,subQ2,subQ1,subQ6,subQ0,subQ10,subQ11])],"isStart":true})});}
            var sketch = newSketch(context, id + "F16", { "sketchPlane" : qUnion([Q0])});
            skLineSegment(sketch, "E79", {"start": v(0, 90) * mm, "end": v(0, 120) * mm, "construction": true});
            skCircle(sketch, "E80", {"center": v(0, 120) * mm, "radius": 6 * mm});
            skLineSegment(sketch, "E81", {"start": v(-15, 120) * mm, "end": v(-15, 108) * mm});
            skLineSegment(sketch, "E82", {"start": v(-15, 108) * mm, "end": v(-33, 90) * mm});
            skArc(sketch, "E83", {"start": v(-15, 120) * mm, "mid": v(0, 135) * mm, "end": v(15, 120) * mm});
            skLineSegment(sketch, "E84", {"start": v(15, 120) * mm, "end": v(15, 108) * mm});
            skLineSegment(sketch, "E85", {"start": v(15, 108) * mm, "end": v(33, 90) * mm});
            skLineSegment(sketch, "E86", {"start": v(-80, 0) * mm, "end": v(80, 0) * mm, "construction": true});
            skArc(sketch, "E87.MirrorCS", {"start": v(15, 120) * mm, "mid": v(0, 135) * mm, "end": v(-15, 120) * mm});
            skLineSegment(sketch, "E88.MirrorCS", {"start": v(80, 0) * mm, "end": v(-80, 0) * mm, "construction": true});
            skArc(sketch, "E89.MirrorCS", {"start": v(15, -120) * mm, "mid": v(0, -135) * mm, "end": v(-15, -120) * mm});
            skLineSegment(sketch, "E90.MirrorCS", {"start": v(15, -120) * mm, "end": v(15, -108) * mm});
            skLineSegment(sketch, "E91.MirrorCS", {"start": v(-15, -120) * mm, "end": v(-15, -108) * mm});
            skLineSegment(sketch, "E92.MirrorCS", {"start": v(-15, -108) * mm, "end": v(-33, -90) * mm});
            skLineSegment(sketch, "E93.MirrorCS", {"start": v(15, -108) * mm, "end": v(33, -90) * mm});
            skCircle(sketch, "E94.MirrorC", {"center": v(0, -120) * mm, "radius": 6 * mm});
            skLineSegment(sketch, "E95.MirrorCS", {"start": v(0, -90) * mm, "end": v(0, -120) * mm, "construction": true});
            skSolve(sketch);
        }
        {
            var Q0;
            Q0 = qSketchRegion(id + "F16", true);
            var Q1;
            Q1=makeQuery(id+"F16.imprint","IMPRINT",FACE,{"disambiguationData":[TD([[makeQuery(id+"F16.imprint","IMPRINT",EDGE,{"derivedFrom":makeQuery(id+"F1.opExtrude","CAP_EDGE",EDGE,{"disambiguationData":[OSD([sQuery(id+"F0.wireOp",EDGE,"E1.left")])],"isStart":true})}),-1.0]])]});
            var Q2;
            Q2=makeQuery(id+"F2.opExtrude","CAP_FACE",FACE,{"disambiguationData":[OSD([sQuery(id+"F0.wireOp",EDGE,"E12"),sQuery(id+"F0.wireOp",EDGE,"E13"),sQuery(id+"F0.wireOp",EDGE,"E14"),sQuery(id+"F0.wireOp",EDGE,"E15"),sQuery(id+"F0.wireOp",EDGE,"E17.filletArc"),sQuery(id+"F0.wireOp",EDGE,"E18.filletArc"),sQuery(id+"F0.wireOp",EDGE,"E19.filletArc"),sQuery(id+"F0.wireOp",EDGE,"E20.filletArc"),sQuery(id+"F0.wireOp",EDGE,"E25.0"),sQuery(id+"F0.wireOp",EDGE,"E25.1"),sQuery(id+"F0.wireOp",EDGE,"E25.2"),sQuery(id+"F0.wireOp",EDGE,"E25.3"),sQuery(id+"F0.wireOp",EDGE,"E25.4"),sQuery(id+"F0.wireOp",EDGE,"E25.5"),sQuery(id+"F0.wireOp",EDGE,"E25.6"),sQuery(id+"F0.wireOp",EDGE,"E25.7")])],"isStart":false});
            var Q3;
            Q3=makeQuery(id+"F2.opExtrude","CAP_FACE",FACE,{"disambiguationData":[OSD([sQuery(id+"F0.wireOp",EDGE,"E12"),sQuery(id+"F0.wireOp",EDGE,"E13"),sQuery(id+"F0.wireOp",EDGE,"E14"),sQuery(id+"F0.wireOp",EDGE,"E15"),sQuery(id+"F0.wireOp",EDGE,"E17.filletArc"),sQuery(id+"F0.wireOp",EDGE,"E18.filletArc"),sQuery(id+"F0.wireOp",EDGE,"E19.filletArc"),sQuery(id+"F0.wireOp",EDGE,"E20.filletArc"),sQuery(id+"F0.wireOp",EDGE,"E25.0"),sQuery(id+"F0.wireOp",EDGE,"E25.1"),sQuery(id+"F0.wireOp",EDGE,"E25.2"),sQuery(id+"F0.wireOp",EDGE,"E25.3"),sQuery(id+"F0.wireOp",EDGE,"E25.4"),sQuery(id+"F0.wireOp",EDGE,"E25.5"),sQuery(id+"F0.wireOp",EDGE,"E25.6"),sQuery(id+"F0.wireOp",EDGE,"E25.7")])],"isStart":false});
            extrude(context, id + "F17", {"entities" : qUnion([Q0, Q1]), "endBound" : BoundingType.UP_TO_SURFACE, "endBoundEntityFace" : qUnion([Q2, Q3]), "depth" : 25 * mm});
        }
    });
